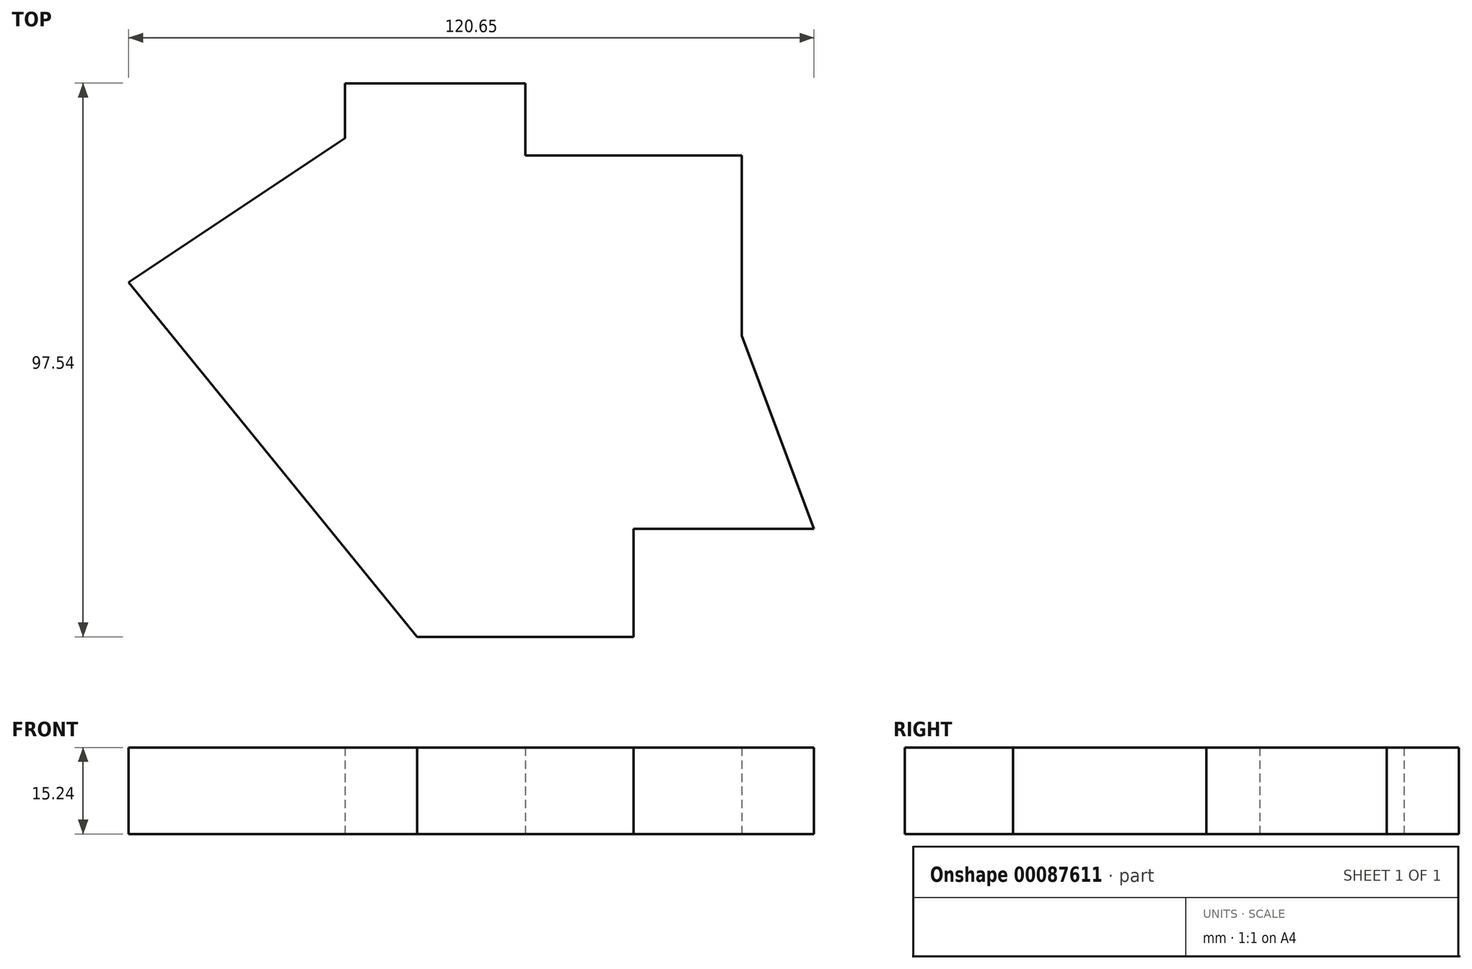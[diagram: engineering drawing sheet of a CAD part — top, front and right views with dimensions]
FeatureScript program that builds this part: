
annotation { "Feature Type Name" : "Feature", "Feature Type Description" : "" }
export const myFeature = defineFeature(function(context is Context, id is Id, definition is map)
    precondition{}
    {
        {
            var Q0;
            Q0=qCreatedBy(makeId("Top.planeOp"),FACE);
            var sketch = newSketch(context, id + "F0", { "sketchPlane" : qUnion([Q0])});
            skLineSegment(sketch, "E0", {"start": v(50.8, 0) * mm, "end": v(0, 62.48) * mm});
            skLineSegment(sketch, "E1", {"start": v(0, 62.48) * mm, "end": v(38.1, 87.88) * mm});
            skLineSegment(sketch, "E2", {"start": v(38.1, 87.88) * mm, "end": v(38.1, 97.54) * mm});
            skLineSegment(sketch, "E3", {"start": v(38.1, 97.54) * mm, "end": v(69.85, 97.54) * mm});
            skLineSegment(sketch, "E4", {"start": v(69.85, 97.54) * mm, "end": v(69.85, 84.84) * mm});
            skLineSegment(sketch, "E5", {"start": v(69.85, 84.84) * mm, "end": v(107.95, 84.84) * mm});
            skLineSegment(sketch, "E6", {"start": v(107.95, 84.84) * mm, "end": v(107.95, 53.09) * mm});
            skLineSegment(sketch, "E7", {"start": v(107.95, 53.09) * mm, "end": v(120.65, 19.05) * mm});
            skLineSegment(sketch, "E8", {"start": v(120.65, 19.05) * mm, "end": v(88.9, 19.05) * mm});
            skLineSegment(sketch, "E9", {"start": v(88.9, 19.05) * mm, "end": v(88.9, 0) * mm});
            skLineSegment(sketch, "E10", {"start": v(88.9, 0) * mm, "end": v(50.8, 0) * mm});
            skSolve(sketch);
        }
        {
            var Q0;
            Q0 = qSketchRegion(id + "F0", true);
            extrude(context, id + "F1", {"entities" : qUnion([Q0]), "depth" : 15.24 * mm});
        }
    });
